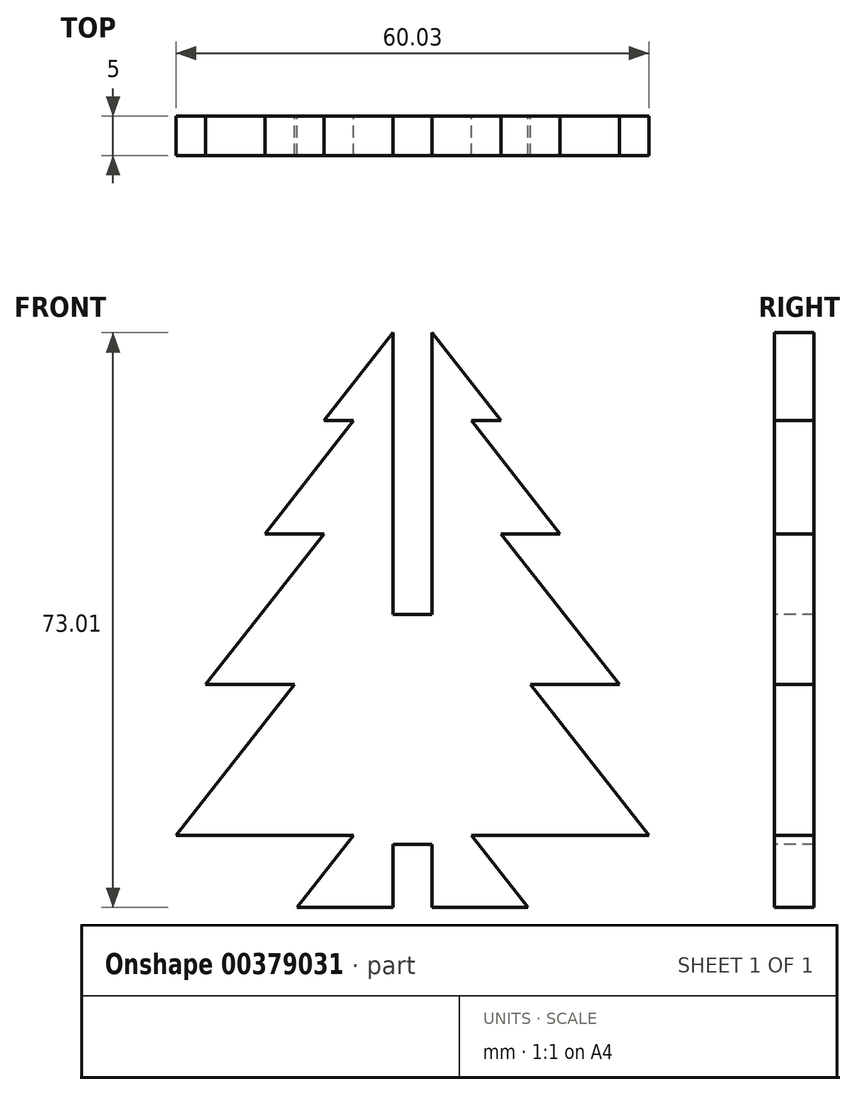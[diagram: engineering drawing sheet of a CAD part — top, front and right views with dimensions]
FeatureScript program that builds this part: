
annotation { "Feature Type Name" : "Feature", "Feature Type Description" : "" }
export const myFeature = defineFeature(function(context is Context, id is Id, definition is map)
    precondition{}
    {
        {
            var Q0;
            Q0=qCreatedBy(makeId("Front.planeOp"),FACE);
            var sketch = newSketch(context, id + "F0", { "sketchPlane" : qUnion([Q0])});
            skLineSegment(sketch, "E0", {"start": v(-0.2, -14.19) * mm, "end": v(7.3, -14.19) * mm});
            skLineSegment(sketch, "E1", {"start": v(7.3, -14.19) * mm, "end": v(-7.7, -14.19) * mm});
            skLineSegment(sketch, "E2", {"start": v(-7.7, -14.19) * mm, "end": v(-7.7, -5.06) * mm});
            skLineSegment(sketch, "E3", {"start": v(7.3, -5.06) * mm, "end": v(-7.7, -5.06) * mm});
            skLineSegment(sketch, "E4", {"start": v(7.3, -5.06) * mm, "end": v(7.3, -14.19) * mm});
            skLineSegment(sketch, "E5", {"start": v(-0.2, -14.19) * mm, "end": v(-0.2, -5.06) * mm});
            skLineSegment(sketch, "E6", {"start": v(-7.7, -5.06) * mm, "end": v(-30.22, -5.06) * mm});
            skLineSegment(sketch, "E7", {"start": v(7.3, -5.06) * mm, "end": v(29.81, -5.06) * mm});
            skLineSegment(sketch, "E8", {"start": v(-30.22, -5.06) * mm, "end": v(-15.21, 14.1) * mm});
            skLineSegment(sketch, "E9", {"start": v(-15.21, 14.1) * mm, "end": v(14.8, 14.1) * mm});
            skLineSegment(sketch, "E10", {"start": v(14.8, 14.1) * mm, "end": v(29.81, -5.06) * mm});
            skLineSegment(sketch, "E11", {"start": v(-0.2, -5.06) * mm, "end": v(-0.2, 14.1) * mm});
            skLineSegment(sketch, "E12", {"start": v(-15.21, 14.1) * mm, "end": v(-26.47, 14.1) * mm});
            skLineSegment(sketch, "E13", {"start": v(-26.47, 14.1) * mm, "end": v(-11.46, 33.27) * mm});
            skLineSegment(sketch, "E14", {"start": v(14.8, 14.1) * mm, "end": v(26.06, 14.1) * mm});
            skLineSegment(sketch, "E15", {"start": v(26.06, 14.1) * mm, "end": v(11.05, 33.27) * mm});
            skLineSegment(sketch, "E16", {"start": v(11.05, 33.27) * mm, "end": v(-11.46, 33.27) * mm});
            skLineSegment(sketch, "E17", {"start": v(-0.2, 14.1) * mm, "end": v(-0.2, 33.27) * mm});
            skLineSegment(sketch, "E18", {"start": v(-11.46, 33.27) * mm, "end": v(-18.96, 33.27) * mm});
            skLineSegment(sketch, "E19", {"start": v(-18.96, 33.27) * mm, "end": v(-7.7, 47.64) * mm});
            skLineSegment(sketch, "E20", {"start": v(-7.7, 47.64) * mm, "end": v(7.3, 47.64) * mm});
            skLineSegment(sketch, "E21", {"start": v(7.3, 47.64) * mm, "end": v(18.56, 33.27) * mm});
            skLineSegment(sketch, "E22", {"start": v(18.56, 33.27) * mm, "end": v(11.05, 33.27) * mm});
            skLineSegment(sketch, "E23", {"start": v(-7.7, 47.64) * mm, "end": v(-11.46, 47.64) * mm});
            skLineSegment(sketch, "E24", {"start": v(-11.46, 47.64) * mm, "end": v(-0.2, 62.01) * mm});
            skLineSegment(sketch, "E25", {"start": v(-0.2, 62.01) * mm, "end": v(11.05, 47.64) * mm});
            skLineSegment(sketch, "E26", {"start": v(11.05, 47.64) * mm, "end": v(7.3, 47.64) * mm});
            skLineSegment(sketch, "E27", {"start": v(-30.22, -5.06) * mm, "end": v(-0.2, -5.06) * mm});
            skLineSegment(sketch, "E28", {"start": v(-0.2, -5.06) * mm, "end": v(29.81, -5.06) * mm});
            skLineSegment(sketch, "E29", {"start": v(-7.7, -14.19) * mm, "end": v(-14.85, -14.19) * mm});
            skLineSegment(sketch, "E30", {"start": v(-14.85, -14.19) * mm, "end": v(-7.7, -5.06) * mm});
            skLineSegment(sketch, "E31", {"start": v(7.3, -14.19) * mm, "end": v(14.45, -14.19) * mm});
            skLineSegment(sketch, "E32", {"start": v(14.45, -14.19) * mm, "end": v(7.3, -5.06) * mm});
            skSolve(sketch);
        }
        {
            var Q0;
            {var subQ0=sQuery(id+"F0.wireOp",EDGE,"E18");Q0=makeQuery(id+"F0.imprint","IMPRINT",FACE,{"disambiguationData":[TD([[makeQuery(id+"F0.imprint","IMPRINT",EDGE,{"derivedFrom":subQ0}),-1.0]])]});}
            var Q1;
            Q1=makeQuery(id+"F0.imprint","IMPRINT",FACE,{"disambiguationData":[TD([[makeQuery(id+"F0.imprint","IMPRINT",EDGE,{"derivedFrom":sQuery(id+"F0.wireOp",EDGE,"E20")}),1.0]])]});
            var Q2;
            {var subQ3=sQuery(id+"F0.wireOp",EDGE,"E12");Q2=makeQuery(id+"F0.imprint","IMPRINT",FACE,{"disambiguationData":[TD([[makeQuery(id+"F0.imprint","IMPRINT",EDGE,{"derivedFrom":subQ3}),-1.0]])]});}
            var Q3;
            {var subQ3=sQuery(id+"F0.wireOp",EDGE,"E14");Q3=makeQuery(id+"F0.imprint","IMPRINT",FACE,{"disambiguationData":[TD([[makeQuery(id+"F0.imprint","IMPRINT",EDGE,{"derivedFrom":subQ3}),1.0]])]});}
            var Q4;
            {var subQ3=sQuery(id+"F0.wireOp",EDGE,"E8");Q4=makeQuery(id+"F0.imprint","IMPRINT",FACE,{"disambiguationData":[TD([[makeQuery(id+"F0.imprint","IMPRINT",EDGE,{"derivedFrom":subQ3}),-1.0]])]});}
            var Q5;
            {var subQ3=sQuery(id+"F0.wireOp",EDGE,"E10");Q5=makeQuery(id+"F0.imprint","IMPRINT",FACE,{"disambiguationData":[TD([[makeQuery(id+"F0.imprint","IMPRINT",EDGE,{"derivedFrom":subQ3}),-1.0]])]});}
            var Q6;
            Q6=makeQuery(id+"F0.imprint","IMPRINT",FACE,{"disambiguationData":[TD([[makeQuery(id+"F0.imprint","IMPRINT",EDGE,{"derivedFrom":sQuery(id+"F0.wireOp",EDGE,"E2")}),1.0]])]});
            var Q7;
            {var subQ0=sQuery(id+"F0.wireOp",EDGE,"E2");Q7=makeQuery(id+"F0.imprint","IMPRINT",FACE,{"disambiguationData":[TD([[makeQuery(id+"F0.imprint","IMPRINT",EDGE,{"derivedFrom":subQ0}),-1.0]])]});}
            var Q8;
            {var subQ0=sQuery(id+"F0.wireOp",EDGE,"E4");Q8=makeQuery(id+"F0.imprint","IMPRINT",FACE,{"disambiguationData":[TD([[makeQuery(id+"F0.imprint","IMPRINT",EDGE,{"derivedFrom":subQ0}),-1.0]])]});}
            var Q9;
            Q9=makeQuery(id+"F0.imprint","IMPRINT",FACE,{"disambiguationData":[TD([[makeQuery(id+"F0.imprint","IMPRINT",EDGE,{"derivedFrom":sQuery(id+"F0.wireOp",EDGE,"E4")}),1.0]])]});
            extrude(context, id + "F1", {"entities" : qUnion([Q0, Q1, Q2, Q3, Q4, Q5, Q6, Q7, Q8, Q9]), "depth" : 5 * mm});
        }
        {
            var Q0;
            Q0=makeQuery(id+"F1.opExtrude","CAP_FACE",FACE,{"disambiguationData":[OSD([sQuery(id+"F0.wireOp",EDGE,"E1"),sQuery(id+"F0.wireOp",EDGE,"E8"),sQuery(id+"F0.wireOp",EDGE,"E10"),sQuery(id+"F0.wireOp",EDGE,"E12"),sQuery(id+"F0.wireOp",EDGE,"E13"),sQuery(id+"F0.wireOp",EDGE,"E14"),sQuery(id+"F0.wireOp",EDGE,"E15"),sQuery(id+"F0.wireOp",EDGE,"E18"),sQuery(id+"F0.wireOp",EDGE,"E19"),sQuery(id+"F0.wireOp",EDGE,"E21"),sQuery(id+"F0.wireOp",EDGE,"E22"),sQuery(id+"F0.wireOp",EDGE,"E23"),sQuery(id+"F0.wireOp",EDGE,"E24"),sQuery(id+"F0.wireOp",EDGE,"E25"),sQuery(id+"F0.wireOp",EDGE,"E26"),sQuery(id+"F0.wireOp",EDGE,"E27"),sQuery(id+"F0.wireOp",EDGE,"E28"),sQuery(id+"F0.wireOp",EDGE,"E29"),sQuery(id+"F0.wireOp",EDGE,"E30"),sQuery(id+"F0.wireOp",EDGE,"E31"),sQuery(id+"F0.wireOp",EDGE,"E32")])],"isStart":false});
            var sketch = newSketch(context, id + "F2", { "sketchPlane" : qUnion([Q0])});
            skLineSegment(sketch, "E33", {"start": v(-0.2, 62.01) * mm, "end": v(-0.2, 23.01) * mm});
            skLineSegment(sketch, "E34.bottom", {"start": v(2.3, 62.01) * mm, "end": v(-2.7, 62.01) * mm});
            skLineSegment(sketch, "E34.top", {"start": v(2.3, 23.01) * mm, "end": v(-2.7, 23.01) * mm});
            skLineSegment(sketch, "E34.left", {"start": v(2.3, 62.01) * mm, "end": v(2.3, 23.01) * mm});
            skLineSegment(sketch, "E34.right", {"start": v(-2.7, 62.01) * mm, "end": v(-2.7, 23.01) * mm});
            skPoint(sketch, "E34.middle", {"position": v(-0.2, 42.51) * mm});
            skLineSegment(sketch, "E35", {"start": v(-0.2, -14.19) * mm, "end": v(-0.2, -6.19) * mm});
            skLineSegment(sketch, "E36.bottom", {"start": v(2.3, -14.19) * mm, "end": v(-2.7, -14.19) * mm});
            skLineSegment(sketch, "E36.top", {"start": v(2.3, -6.19) * mm, "end": v(-2.7, -6.19) * mm});
            skLineSegment(sketch, "E36.left", {"start": v(2.3, -14.19) * mm, "end": v(2.3, -6.19) * mm});
            skLineSegment(sketch, "E36.right", {"start": v(-2.7, -14.19) * mm, "end": v(-2.7, -6.19) * mm});
            skPoint(sketch, "E36.middle", {"position": v(-0.2, -10.19) * mm});
            skSolve(sketch);
        }
        {
            var Q0;
            {var subQ0=sQuery(id+"F2.wireOp",EDGE,"E33");Q0=makeQuery(id+"F2.imprint","IMPRINT",FACE,{"disambiguationData":[TD([[makeQuery(id+"F2.imprint","IMPRINT",EDGE,{"derivedFrom":subQ0}),-1.0]])]});}
            var Q1;
            {var subQ0=sQuery(id+"F2.wireOp",EDGE,"E33");Q1=makeQuery(id+"F2.imprint","IMPRINT",FACE,{"disambiguationData":[TD([[makeQuery(id+"F2.imprint","IMPRINT",EDGE,{"derivedFrom":subQ0}),1.0]])]});}
            var Q2;
            {var subQ0=sQuery(id+"F2.wireOp",EDGE,"E35");Q2=makeQuery(id+"F2.imprint","IMPRINT",FACE,{"disambiguationData":[TD([[makeQuery(id+"F2.imprint","IMPRINT",EDGE,{"derivedFrom":subQ0}),1.0]])]});}
            var Q3;
            {var subQ0=sQuery(id+"F2.wireOp",EDGE,"E35");Q3=makeQuery(id+"F2.imprint","IMPRINT",FACE,{"disambiguationData":[TD([[makeQuery(id+"F2.imprint","IMPRINT",EDGE,{"derivedFrom":subQ0}),-1.0]])]});}
            extrude(context, id + "F3", {"entities" : qUnion([Q0, Q1, Q2, Q3]), "operationType" : NewBodyOperationType.REMOVE, "oppositeDirection" : true, "depth" : 25 * mm});
        }
    });
